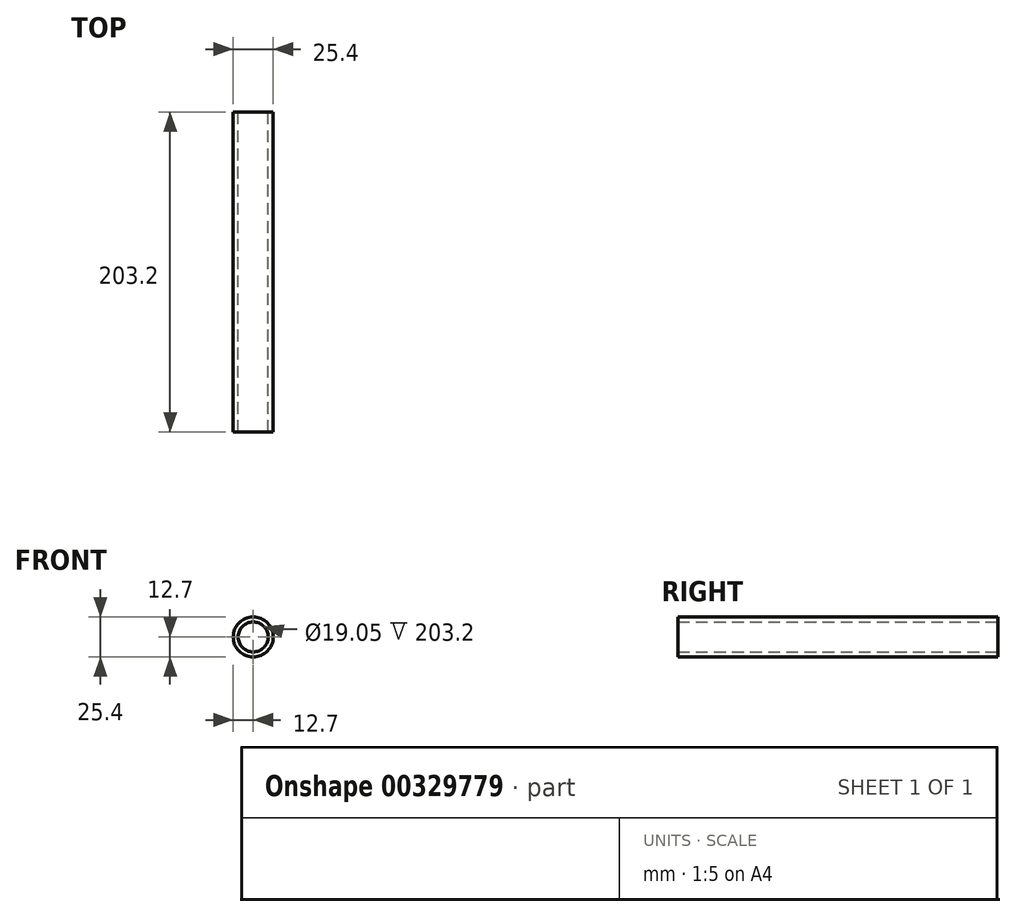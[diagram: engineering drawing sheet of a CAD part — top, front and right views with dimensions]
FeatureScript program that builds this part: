
annotation { "Feature Type Name" : "Feature", "Feature Type Description" : "" }
export const myFeature = defineFeature(function(context is Context, id is Id, definition is map)
    precondition{}
    {
        {
            var Q0;
            Q0=qCreatedBy(makeId("Front.planeOp"),FACE);
            var sketch = newSketch(context, id + "F0", { "sketchPlane" : qUnion([Q0])});
            skCircle(sketch, "E0", {"center": v(0, 0) * mm, "radius": 12.7 * mm});
            skSolve(sketch);
        }
        {
            var Q0;
            Q0 = qSketchRegion(id + "F0", true);
            extrude(context, id + "F1", {"entities" : qUnion([Q0]), "endBound" : BoundingType.SYMMETRIC, "depth" : 203.2 * mm});
        }
        {
            var Q0;
            Q0=sQuery(id+"F0.wireOp",VERTEX,"E0.center");
            var Q1;
            Q1=makeQuery(id+"F1.opExtrude","SWEPT_BODY",BODY,{"disambiguationData":[OSD([sQuery(id+"F0.wireOp",EDGE,"E0")])]});
            hole(context, id + "F2", {"style" : HoleStyle.SIMPLE, "endStyle" : HoleEndStyle.THROUGH, "oppositeDirection" : true, "holeDiameter" : 19.05 * mm, "tappedDepth" : 12.7 * mm, "tapClearance" : 3, "locations" : qUnion([Q0]), "scope" : qUnion([Q1])});
        }
        {
            var Q0;
            Q0=sQuery(id+"F0.wireOp",VERTEX,"E0.center");
            var Q1;
            Q1=makeQuery(id+"F1.opExtrude","SWEPT_BODY",BODY,{"disambiguationData":[OSD([sQuery(id+"F0.wireOp",EDGE,"E0")])]});
            hole(context, id + "F3", {"style" : HoleStyle.SIMPLE, "endStyle" : HoleEndStyle.THROUGH, "holeDiameter" : 19.05 * mm, "tappedDepth" : 12.7 * mm, "tapClearance" : 3, "locations" : qUnion([Q0]), "scope" : qUnion([Q1])});
        }
    });
